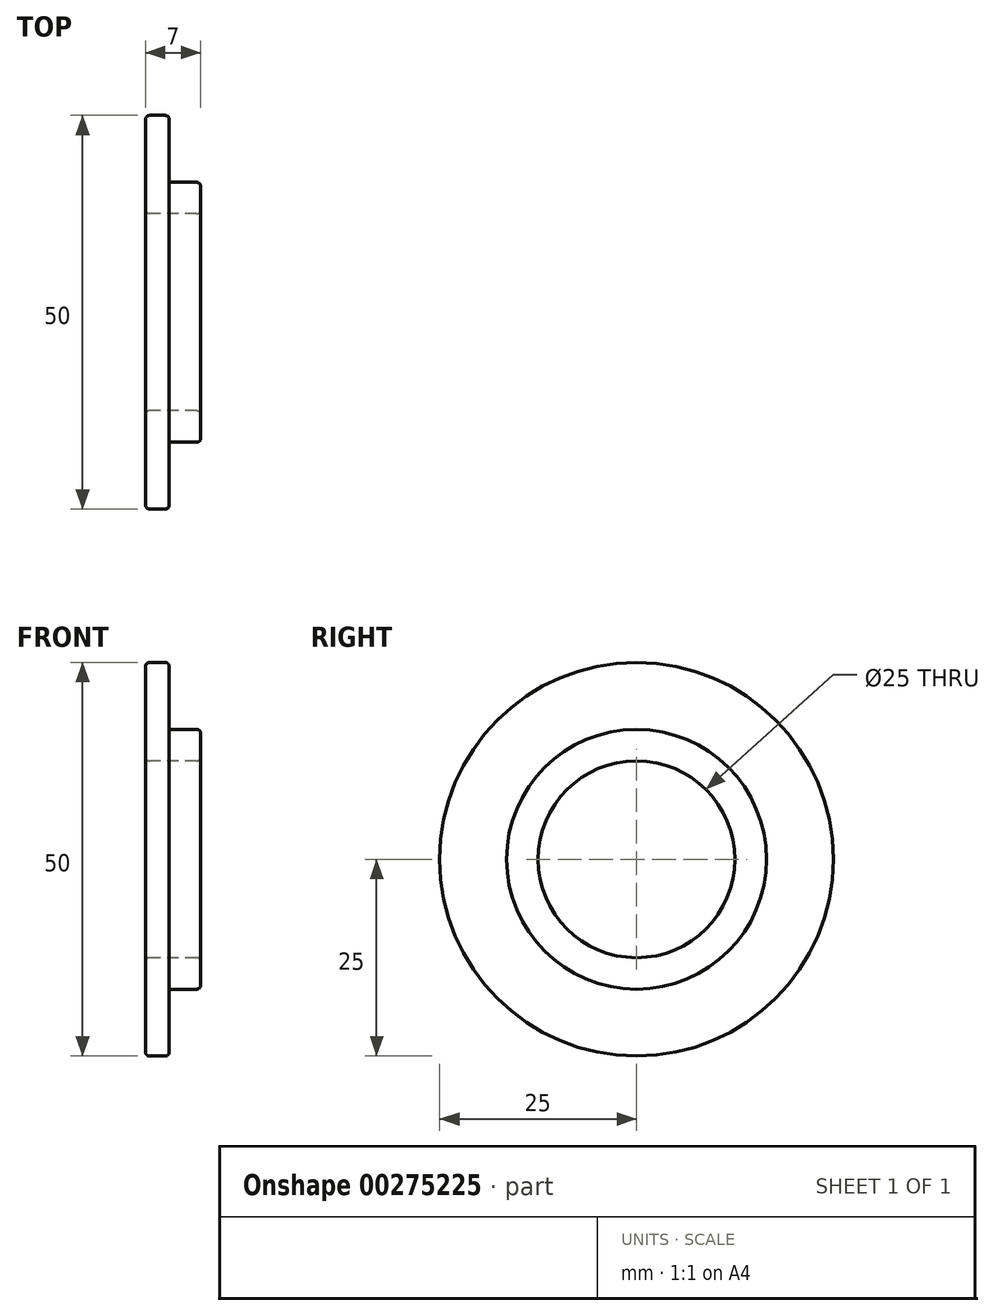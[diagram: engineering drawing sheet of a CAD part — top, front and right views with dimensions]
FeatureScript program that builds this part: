
annotation { "Feature Type Name" : "Feature", "Feature Type Description" : "" }
export const myFeature = defineFeature(function(context is Context, id is Id, definition is map)
    precondition{}
    {
        {
            var Q0;
            Q0=qCreatedBy(makeId("Front.planeOp"),FACE);
            var sketch = newSketch(context, id + "F0", { "sketchPlane" : qUnion([Q0])});
            skLineSegment(sketch, "E0", {"start": v(0, 12.5) * mm, "end": v(0, 25) * mm});
            skLineSegment(sketch, "E1", {"start": v(0, 25) * mm, "end": v(3, 25) * mm});
            skLineSegment(sketch, "E2", {"start": v(3, 25) * mm, "end": v(3, 16.5) * mm});
            skLineSegment(sketch, "E3", {"start": v(3, 16.5) * mm, "end": v(7, 16.5) * mm});
            skLineSegment(sketch, "E4", {"start": v(7, 16.5) * mm, "end": v(7, 12.5) * mm});
            skLineSegment(sketch, "E5", {"start": v(7, 12.5) * mm, "end": v(0, 12.5) * mm});
            skLineSegment(sketch, "E6.MirrorCS", {"start": v(3, -25) * mm, "end": v(3, -16.5) * mm, "construction": true});
            skLineSegment(sketch, "E7.MirrorCS", {"start": v(0, -25) * mm, "end": v(3, -25) * mm, "construction": true});
            skLineSegment(sketch, "E8.MirrorCS", {"start": v(7, -12.5) * mm, "end": v(0, -12.5) * mm, "construction": true});
            skLineSegment(sketch, "E9.MirrorCS", {"start": v(3, -16.5) * mm, "end": v(7, -16.5) * mm, "construction": true});
            skLineSegment(sketch, "E10.MirrorCS", {"start": v(0, -12.5) * mm, "end": v(0, -25) * mm, "construction": true});
            skLineSegment(sketch, "E11.MirrorCS", {"start": v(7, -16.5) * mm, "end": v(7, -12.5) * mm, "construction": true});
            skLineSegment(sketch, "E12", {"start": v(-40.5, 0) * mm, "end": v(37.06, 0) * mm, "construction": true});
            skSolve(sketch);
        }
        {
            var Q0;
            Q0=makeQuery(id+"F0.imprint","IMPRINT",FACE,{"disambiguationData":[TD([[makeQuery(id+"F0.imprint","IMPRINT",EDGE,{"derivedFrom":sQuery(id+"F0.wireOp",EDGE,"E0")}),-1.0]])]});
            var Q1;
            Q1=sQuery(id+"F0.wireOp",EDGE,"E12");
            revolve(context, id + "F1", {"entities" : qUnion([Q0]), "axis" : qUnion([Q1]), "revolveType" : RevolveType.FULL});
        }
        {
            var Q0;
            Q0=makeQuery(id+"F1.opRevolve","SWEPT_EDGE",EDGE,{"disambiguationData":[OSD([sQuery(id+"F0.wireOp",EDGE,"E0"),sQuery(id+"F0.wireOp",EDGE,"E1")])]});
            var Q1;
            Q1=makeQuery(id+"F1.opRevolve","SWEPT_EDGE",EDGE,{"disambiguationData":[OSD([sQuery(id+"F0.wireOp",EDGE,"E1"),sQuery(id+"F0.wireOp",EDGE,"E2")])]});
            var Q2;
            Q2=makeQuery(id+"F1.opRevolve","SWEPT_EDGE",EDGE,{"disambiguationData":[OSD([sQuery(id+"F0.wireOp",EDGE,"E3"),sQuery(id+"F0.wireOp",EDGE,"E4")])]});
            var Q3;
            Q3=makeQuery(id+"F1.opRevolve","SWEPT_EDGE",EDGE,{"disambiguationData":[OSD([sQuery(id+"F0.wireOp",EDGE,"E4"),sQuery(id+"F0.wireOp",EDGE,"E5")])]});
            var Q4;
            Q4=makeQuery(id+"F1.opRevolve","SWEPT_EDGE",EDGE,{"disambiguationData":[OSD([sQuery(id+"F0.wireOp",EDGE,"E0"),sQuery(id+"F0.wireOp",EDGE,"E5")])]});
            fillet(context, id + "F2", {"entities" : qUnion([Q0, Q1, Q2, Q3, Q4]), "radius" : .5 * mm, "tangentPropagation" : true, "allowEdgeOverflow" : false});
        }
    });
